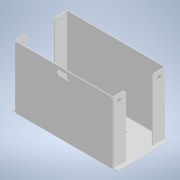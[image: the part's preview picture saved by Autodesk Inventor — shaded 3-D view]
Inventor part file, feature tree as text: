
AUTODESK INVENTOR PART (.ipt)
format: ipt  version: 2022 (Build 260153000, 153)  size: 313,856 bytes
history: native  units: mm
features: other x17, sketch x5, reference x2, projected_geometry x2, fillet x1
ambient origin geometry x8: Origin, YZ Plane, XZ Plane, XY Plane, X Axis, Y Axis, Z Axis, Center Point
bodies: Body1 (feature_tree)
feature tree (27):
  other  "Твердое тело1"
  other  "Грань1"
  other  "Фланец2"
  other  "Фланец4"
  fillet  "Сопряжение1"  Radius=0.5mm
  sketch  "Эскиз1"
  other  "Пластина1"
  sketch  "Эскиз3"
  other  "Пластина3"
  other  "Сгиб2"
  other  "УглСтык2"
  sketch  "Эскиз4"
  sketch  "Эскиз8"
  other  "Пластина5"
  other  "Сгиб4"
  other  "УглСтык4"
  sketch  "Эскиз9"
  reference  "Ссылка1"
  reference  "Ссылка2"
  other  "Вырез1"
  other  "Вырез4"
  other  "Определение1"
  other  "<userpath>\Documents\Git\MZCAT_battery\FastBattery2.iam"
  other  "FastBattery2.iam"
  other  "akkum_base2_2:1"
  projected_geometry  "Спроецированная петля1"
  projected_geometry  "Спроецированная петля2"
